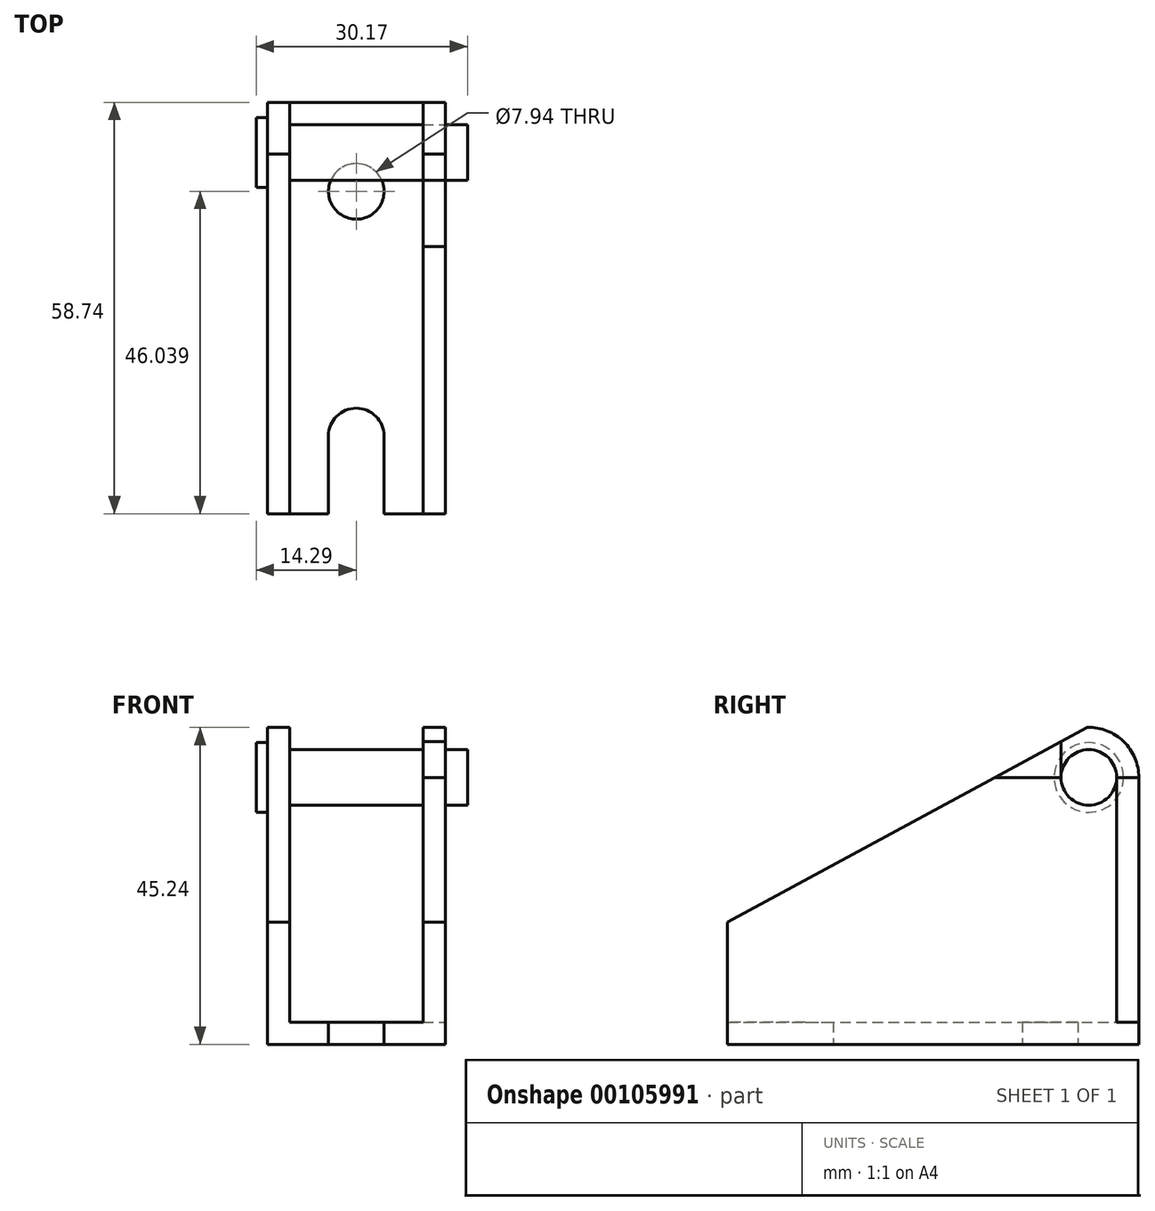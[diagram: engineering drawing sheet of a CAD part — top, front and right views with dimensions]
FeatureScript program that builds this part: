
annotation { "Feature Type Name" : "Feature", "Feature Type Description" : "" }
export const myFeature = defineFeature(function(context is Context, id is Id, definition is map)
    precondition{}
    {
        {
            var Q0;
            Q0=qCreatedBy(makeId("Top.planeOp"),FACE);
            var sketch = newSketch(context, id + "F0", { "sketchPlane" : qUnion([Q0])});
            skLineSegment(sketch, "E0.bottom", {"start": v(-12.7, 29.37) * mm, "end": v(12.7, 29.37) * mm});
            skLineSegment(sketch, "E0.top", {"start": v(-12.7, -29.37) * mm, "end": v(12.7, -29.37) * mm});
            skLineSegment(sketch, "E0.left", {"start": v(-12.7, 29.37) * mm, "end": v(-12.7, -29.37) * mm});
            skLineSegment(sketch, "E0.right", {"start": v(12.7, 29.37) * mm, "end": v(12.7, -29.37) * mm});
            skLineSegment(sketch, "E1", {"start": v(0, 29.37) * mm, "end": v(0, -30.48) * mm, "construction": true});
            skPoint(sketch, "E1.endSnap0", {"position": v(0, -29.37) * mm});
            skLineSegment(sketch, "E2", {"start": v(-12.7, 16.67) * mm, "end": v(12.7, 16.67) * mm, "construction": true});
            skLineSegment(sketch, "E3", {"start": v(-12.7, -18.26) * mm, "end": v(12.7, -18.26) * mm, "construction": true});
            skCircle(sketch, "E4", {"center": v(0, 16.67) * mm, "radius": 3.97 * mm});
            skCircle(sketch, "E5", {"center": v(0, -18.26) * mm, "radius": 3.97 * mm});
            skLineSegment(sketch, "E6", {"start": v(-3.97, -18.26) * mm, "end": v(-3.97, -29.37) * mm});
            skLineSegment(sketch, "E7", {"start": v(3.97, -18.26) * mm, "end": v(3.97, -29.37) * mm});
            skSolve(sketch);
        }
        {
            var Q0;
            Q0=makeQuery(id+"F0.imprint","IMPRINT",FACE,{"disambiguationData":[TD([[makeQuery(id+"F0.imprint","IMPRINT",EDGE,{"derivedFrom":sQuery(id+"F0.wireOp",EDGE,"E0.bottom")}),-1.0]])]});
            extrude(context, id + "F1", {"entities" : qUnion([Q0]), "depth" : 3.17 * mm});
        }
        {
            var Q0;
            Q0=makeQuery(id+"F1.opExtrude","SWEPT_FACE",FACE,{"disambiguationData":[OSD([sQuery(id+"F0.wireOp",EDGE,"E0.left")])]});
            var sketch = newSketch(context, id + "F2", { "sketchPlane" : qUnion([Q0])});
            skLineSegment(sketch, "E8.bottom", {"start": v(-29.37, 0) * mm, "end": v(29.37, 0) * mm});
            skLineSegment(sketch, "E8.top", {"start": v(-29.37, 17.46) * mm, "end": v(29.37, 17.46) * mm});
            skLineSegment(sketch, "E8.left", {"start": v(-29.37, 0) * mm, "end": v(-29.37, 17.46) * mm});
            skLineSegment(sketch, "E8.right", {"start": v(29.37, 0) * mm, "end": v(29.37, 17.46) * mm});
            skLineSegment(sketch, "E9", {"start": v(-29.37, 0) * mm, "end": v(-29.37, 38.1) * mm});
            skPoint(sketch, "E10", {"position": v(-29.37, 38.1) * mm});
            skLineSegment(sketch, "E11", {"start": v(-29.37, 38.1) * mm, "end": v(-8.81, 38.1) * mm, "construction": true});
            skPoint(sketch, "E12", {"position": v(-26.2, 0) * mm});
            skPoint(sketch, "E13", {"position": v(-18.26, 0) * mm});
            skLineSegment(sketch, "E14", {"start": v(-26.2, 0) * mm, "end": v(-26.2, 44.04) * mm, "construction": true});
            skLineSegment(sketch, "E15", {"start": v(-18.26, 0) * mm, "end": v(-18.26, 43.2) * mm, "construction": true});
            skPoint(sketch, "E16", {"position": v(-22.23, 0) * mm});
            skLineSegment(sketch, "E17", {"start": v(-22.23, 0) * mm, "end": v(-22.23, 45.35) * mm, "construction": true});
            skCircle(sketch, "E18", {"center": v(-22.23, 38.1) * mm, "radius": 3.97 * mm});
            skArc(sketch, "E19", {"start": v(-22.02, 45.24) * mm, "mid": v(-27.2, 43.22) * mm, "end": v(-29.37, 38.1) * mm});
            skLineSegment(sketch, "E20.trimOffspring", {"start": v(-22.22, 45.35) * mm, "end": v(29.37, 17.46) * mm});
            skPoint(sketch, "E21.start.orphan", {"position": v(-29.37, 49.21) * mm});
            skLineSegment(sketch, "E22", {"start": v(-29.37, 0) * mm, "end": v(-29.37, 49.21) * mm, "construction": true});
            skLineSegment(sketch, "E23", {"start": v(29.37, 17.46) * mm, "end": v(-29.37, 49.21) * mm, "construction": true});
            skCircle(sketch, "E24", {"center": v(-22.23, 38.1) * mm, "radius": 4.97 * mm});
            skSolve(sketch);
        }
        {
            var Q0;
            {var subQ1=sQuery(id+"F2.wireOp",EDGE,"E8.top");Q0=makeQuery(id+"F2.imprint","IMPRINT",FACE,{"disambiguationData":[TD([[makeQuery(id+"F2.imprint","IMPRINT",EDGE,{"derivedFrom":subQ1}),1.0]])]});}
            var Q1;
            {var subQ0=sQuery(id+"F2.wireOp",EDGE,"E8.top");Q1=makeQuery(id+"F2.imprint","IMPRINT",FACE,{"disambiguationData":[TD([[makeQuery(id+"F2.imprint","IMPRINT",EDGE,{"derivedFrom":subQ0}),-1.0]])]});}
            var Q2;
            {var subQ0=sQuery(id+"F2.wireOp",EDGE,"E8.bottom");Q2=makeQuery(id+"F2.imprint","IMPRINT",FACE,{"disambiguationData":[TD([[makeQuery(id+"F2.imprint","IMPRINT",EDGE,{"derivedFrom":subQ0}),1.0]])]});}
            var Q3;
            Q3=makeQuery(id+"F2.imprint","IMPRINT",FACE,{"disambiguationData":[TD([[makeQuery(id+"F2.imprint","IMPRINT",EDGE,{"derivedFrom":sQuery(id+"F2.wireOp",EDGE,"E18")}),-1.0]])]});
            extrude(context, id + "F3", {"entities" : qUnion([Q0, Q1, Q2, Q3]), "operationType" : NewBodyOperationType.ADD, "oppositeDirection" : true, "depth" : 3.17 * mm});
        }
        {
            var Q0;
            Q0=makeQuery(id+"F1.opExtrude","SWEPT_FACE",FACE,{"disambiguationData":[OSD([sQuery(id+"F0.wireOp",EDGE,"E0.right")])]});
            var sketch = newSketch(context, id + "F4", { "sketchPlane" : qUnion([Q0])});
            skLineSegment(sketch, "E25.0", {"start": v(29.37, 0) * mm, "end": v(-29.37, 0) * mm});
            skLineSegment(sketch, "E25.1", {"start": v(29.37, 17.46) * mm, "end": v(-29.37, 17.46) * mm});
            skLineSegment(sketch, "E25.2", {"start": v(29.37, 0) * mm, "end": v(29.37, 17.46) * mm});
            skLineSegment(sketch, "E25.3", {"start": v(-29.37, 0) * mm, "end": v(-29.37, 17.46) * mm});
            skLineSegment(sketch, "E25.4", {"start": v(29.37, 0) * mm, "end": v(29.37, 38.1) * mm});
            skPoint(sketch, "E25.5", {"position": v(29.37, 38.1) * mm});
            skLineSegment(sketch, "E25.6", {"start": v(29.37, 38.1) * mm, "end": v(8.81, 38.1) * mm});
            skPoint(sketch, "E25.7", {"position": v(26.2, 0) * mm});
            skPoint(sketch, "E25.8", {"position": v(18.26, 0) * mm});
            skLineSegment(sketch, "E25.9", {"start": v(26.2, 0) * mm, "end": v(26.2, 44.04) * mm});
            skLineSegment(sketch, "E25.10", {"start": v(18.26, 0) * mm, "end": v(18.26, 43.2) * mm});
            skPoint(sketch, "E25.11", {"position": v(22.23, 0) * mm});
            skLineSegment(sketch, "E25.12", {"start": v(22.23, 0) * mm, "end": v(22.23, 45.35) * mm});
            skCircle(sketch, "E25.13", {"center": v(22.23, 38.1) * mm, "radius": 3.97 * mm});
            skArc(sketch, "E25.14", {"start": v(22.02, 45.24) * mm, "mid": v(27.2, 43.22) * mm, "end": v(29.37, 38.1) * mm});
            skLineSegment(sketch, "E25.15", {"start": v(22.22, 45.35) * mm, "end": v(-29.37, 17.46) * mm});
            skPoint(sketch, "E25.16", {"position": v(29.37, 49.21) * mm});
            skLineSegment(sketch, "E25.17", {"start": v(29.37, 0) * mm, "end": v(29.37, 49.21) * mm});
            skLineSegment(sketch, "E25.18", {"start": v(-29.37, 17.46) * mm, "end": v(29.37, 49.21) * mm});
            skLineSegment(sketch, "E25.19", {"start": v(22.02, 45.24) * mm, "end": v(-29.37, 17.46) * mm});
            skSolve(sketch);
        }
        {
            var Q0;
            {var subQ1=sQuery(id+"F4.wireOp",EDGE,"E25.1");var subQ3=sQuery(id+"F4.wireOp",EDGE,"E25.10");var subQ4=makeQuery(id+"F4.imprint","INTERSECT",VERTEX,{"derivedFrom":[subQ1,subQ3]});Q0=makeQuery(id+"F4.imprint","IMPRINT",FACE,{"disambiguationData":[TD([[makeQuery(id+"F4.imprint","IMPRINT",EDGE,{"disambiguationData":[TD([[subQ4,-1.0]])],"derivedFrom":subQ1}),-1.0]])]});}
            var Q1;
            {var subQ0=sQuery(id+"F4.wireOp",EDGE,"E25.19");var subQ1=sQuery(id+"F4.wireOp",EDGE,"E25.6");var subQ2=makeQuery(id+"F4.imprint","INTERSECT",VERTEX,{"derivedFrom":[subQ1,subQ0]});Q1=makeQuery(id+"F4.imprint","IMPRINT",FACE,{"disambiguationData":[TD([[makeQuery(id+"F4.imprint","IMPRINT",EDGE,{"disambiguationData":[TD([[subQ2,1.0]])],"derivedFrom":subQ0}),1.0]])]});}
            var Q2;
            {var subQ3=sQuery(id+"F4.wireOp",EDGE,"E25.12");var subQ5=sQuery(id+"F4.wireOp",EDGE,"E25.13");var subQ6=makeQuery(id+"F4.imprint","INTERSECT",VERTEX,{"disambiguationData":[OD(1.0)],"derivedFrom":[subQ3,subQ5]});Q2=makeQuery(id+"F4.imprint","IMPRINT",FACE,{"disambiguationData":[TD([[makeQuery(id+"F4.imprint","IMPRINT",EDGE,{"disambiguationData":[TD([[subQ6,-1.0]])],"derivedFrom":subQ3}),1.0]])]});}
            var Q3;
            {var subQ3=sQuery(id+"F4.wireOp",EDGE,"E25.13");var subQ5=sQuery(id+"F4.wireOp",EDGE,"E25.12");var subQ6=makeQuery(id+"F4.imprint","INTERSECT",VERTEX,{"disambiguationData":[OD(1.0)],"derivedFrom":[subQ5,subQ3]});Q3=makeQuery(id+"F4.imprint","IMPRINT",FACE,{"disambiguationData":[TD([[makeQuery(id+"F4.imprint","IMPRINT",EDGE,{"disambiguationData":[TD([[subQ6,-1.0]])],"derivedFrom":subQ5}),-1.0]])]});}
            var Q4;
            {var subQ0=sQuery(id+"F4.wireOp",EDGE,"E25.14");var subQ3=sQuery(id+"F4.wireOp",EDGE,"E25.9");var subQ5=makeQuery(id+"F4.imprint","INTERSECT",VERTEX,{"derivedFrom":[subQ3,subQ0]});Q4=makeQuery(id+"F4.imprint","IMPRINT",FACE,{"disambiguationData":[TD([[makeQuery(id+"F4.imprint","IMPRINT",EDGE,{"disambiguationData":[TD([[subQ5,1.0]])],"derivedFrom":subQ3}),-1.0]])]});}
            var Q5;
            {var subQ0=sQuery(id+"F4.wireOp",EDGE,"E25.17");var subQ1=sQuery(id+"F4.wireOp",EDGE,"E25.1");var subQ2=makeQuery(id+"F4.imprint","INTERSECT",VERTEX,{"derivedFrom":[subQ1,subQ0]});Q5=makeQuery(id+"F4.imprint","IMPRINT",FACE,{"disambiguationData":[TD([[makeQuery(id+"F4.imprint","IMPRINT",EDGE,{"disambiguationData":[TD([[subQ2,-1.0]])],"derivedFrom":subQ1}),-1.0]])]});}
            var Q6;
            {var subQ0=sQuery(id+"F4.wireOp",EDGE,"E25.9");var subQ1=sQuery(id+"F4.wireOp",EDGE,"E25.1");var subQ2=makeQuery(id+"F4.imprint","INTERSECT",VERTEX,{"derivedFrom":[subQ1,subQ0]});Q6=makeQuery(id+"F4.imprint","IMPRINT",FACE,{"disambiguationData":[TD([[makeQuery(id+"F4.imprint","IMPRINT",EDGE,{"disambiguationData":[TD([[subQ2,-1.0]])],"derivedFrom":subQ1}),-1.0]])]});}
            var Q7;
            {var subQ0=sQuery(id+"F4.wireOp",EDGE,"E25.12");var subQ1=sQuery(id+"F4.wireOp",EDGE,"E25.1");var subQ2=makeQuery(id+"F4.imprint","INTERSECT",VERTEX,{"derivedFrom":[subQ1,subQ0]});Q7=makeQuery(id+"F4.imprint","IMPRINT",FACE,{"disambiguationData":[TD([[makeQuery(id+"F4.imprint","IMPRINT",EDGE,{"disambiguationData":[TD([[subQ2,-1.0]])],"derivedFrom":subQ1}),-1.0]])]});}
            var Q8;
            {var subQ0=sQuery(id+"F4.wireOp",EDGE,"E25.12");var subQ1=sQuery(id+"F4.wireOp",EDGE,"E25.1");var subQ2=makeQuery(id+"F4.imprint","INTERSECT",VERTEX,{"derivedFrom":[subQ1,subQ0]});Q8=makeQuery(id+"F4.imprint","IMPRINT",FACE,{"disambiguationData":[TD([[makeQuery(id+"F4.imprint","IMPRINT",EDGE,{"disambiguationData":[TD([[subQ2,-1.0]])],"derivedFrom":subQ1}),1.0]])]});}
            var Q9;
            {var subQ0=sQuery(id+"F4.wireOp",EDGE,"E25.9");var subQ1=sQuery(id+"F4.wireOp",EDGE,"E25.1");var subQ2=makeQuery(id+"F4.imprint","INTERSECT",VERTEX,{"derivedFrom":[subQ1,subQ0]});Q9=makeQuery(id+"F4.imprint","IMPRINT",FACE,{"disambiguationData":[TD([[makeQuery(id+"F4.imprint","IMPRINT",EDGE,{"disambiguationData":[TD([[subQ2,-1.0]])],"derivedFrom":subQ1}),1.0]])]});}
            var Q10;
            {var subQ0=sQuery(id+"F4.wireOp",EDGE,"E25.17");var subQ1=sQuery(id+"F4.wireOp",EDGE,"E25.1");var subQ2=makeQuery(id+"F4.imprint","INTERSECT",VERTEX,{"derivedFrom":[subQ1,subQ0]});Q10=makeQuery(id+"F4.imprint","IMPRINT",FACE,{"disambiguationData":[TD([[makeQuery(id+"F4.imprint","IMPRINT",EDGE,{"disambiguationData":[TD([[subQ2,-1.0]])],"derivedFrom":subQ1}),1.0]])]});}
            var Q11;
            {var subQ0=sQuery(id+"F4.wireOp",EDGE,"E25.17");var subQ1=sQuery(id+"F4.wireOp",EDGE,"E25.0");var subQ2=makeQuery(id+"F4.imprint","INTERSECT",VERTEX,{"derivedFrom":[subQ1,subQ0]});Q11=makeQuery(id+"F4.imprint","IMPRINT",FACE,{"disambiguationData":[TD([[makeQuery(id+"F4.imprint","IMPRINT",EDGE,{"disambiguationData":[TD([[subQ2,-1.0]])],"derivedFrom":subQ1}),-1.0]])]});}
            var Q12;
            {var subQ0=sQuery(id+"F4.wireOp",EDGE,"E25.9");var subQ1=sQuery(id+"F4.wireOp",EDGE,"E25.0");var subQ2=makeQuery(id+"F4.imprint","INTERSECT",VERTEX,{"derivedFrom":[subQ1,subQ0]});Q12=makeQuery(id+"F4.imprint","IMPRINT",FACE,{"disambiguationData":[TD([[makeQuery(id+"F4.imprint","IMPRINT",EDGE,{"disambiguationData":[TD([[subQ2,-1.0]])],"derivedFrom":subQ1}),-1.0]])]});}
            var Q13;
            {var subQ0=sQuery(id+"F4.wireOp",EDGE,"E25.10");var subQ1=sQuery(id+"F4.wireOp",EDGE,"E25.0");var subQ2=makeQuery(id+"F4.imprint","INTERSECT",VERTEX,{"derivedFrom":[subQ1,subQ0]});Q13=makeQuery(id+"F4.imprint","IMPRINT",FACE,{"disambiguationData":[TD([[makeQuery(id+"F4.imprint","IMPRINT",EDGE,{"disambiguationData":[TD([[subQ2,1.0]])],"derivedFrom":subQ1}),-1.0]])]});}
            var Q14;
            {var subQ0=sQuery(id+"F4.wireOp",EDGE,"E25.3");var subQ1=sQuery(id+"F4.wireOp",EDGE,"E25.0");var subQ2=makeQuery(id+"F4.imprint","INTERSECT",VERTEX,{"derivedFrom":[subQ1,subQ0]});Q14=makeQuery(id+"F4.imprint","IMPRINT",FACE,{"disambiguationData":[TD([[makeQuery(id+"F4.imprint","IMPRINT",EDGE,{"disambiguationData":[TD([[subQ2,1.0]])],"derivedFrom":subQ1}),-1.0]])]});}
            var Q15;
            {var subQ1=sQuery(id+"F4.wireOp",EDGE,"E25.1");var subQ3=sQuery(id+"F4.wireOp",EDGE,"E25.10");var subQ4=makeQuery(id+"F4.imprint","INTERSECT",VERTEX,{"derivedFrom":[subQ1,subQ3]});Q15=makeQuery(id+"F4.imprint","IMPRINT",FACE,{"disambiguationData":[TD([[makeQuery(id+"F4.imprint","IMPRINT",EDGE,{"disambiguationData":[TD([[subQ4,1.0]])],"derivedFrom":subQ3}),1.0]])]});}
            extrude(context, id + "F5", {"entities" : qUnion([Q0, Q1, Q2, Q3, Q4, Q5, Q6, Q7, Q8, Q9, Q10, Q11, Q12, Q13, Q14, Q15]), "operationType" : NewBodyOperationType.ADD, "oppositeDirection" : true, "depth" : 3.17 * mm});
        }
        {
            var Q0;
            Q0=makeQuery(id+"F2.imprint","IMPRINT",FACE,{"disambiguationData":[TD([[makeQuery(id+"F2.imprint","IMPRINT",EDGE,{"derivedFrom":sQuery(id+"F2.wireOp",EDGE,"E18")}),1.0]])]});
            extrude(context, id + "F6", {"entities" : qUnion([Q0]), "operationType" : NewBodyOperationType.ADD, "oppositeDirection" : true, "depth" : 28.57 * mm});
        }
        {
            var Q0;
            Q0=makeQuery(id+"F2.imprint","IMPRINT",FACE,{"disambiguationData":[TD([[makeQuery(id+"F2.imprint","IMPRINT",EDGE,{"derivedFrom":sQuery(id+"F2.wireOp",EDGE,"E18")}),1.0]])]});
            var Q1;
            Q1=makeQuery(id+"F2.imprint","IMPRINT",FACE,{"disambiguationData":[TD([[makeQuery(id+"F2.imprint","IMPRINT",EDGE,{"derivedFrom":sQuery(id+"F2.wireOp",EDGE,"E18")}),-1.0]])]});
            extrude(context, id + "F7", {"entities" : qUnion([Q0, Q1]), "operationType" : NewBodyOperationType.ADD, "depth" : 1.59 * mm});
        }
    });
